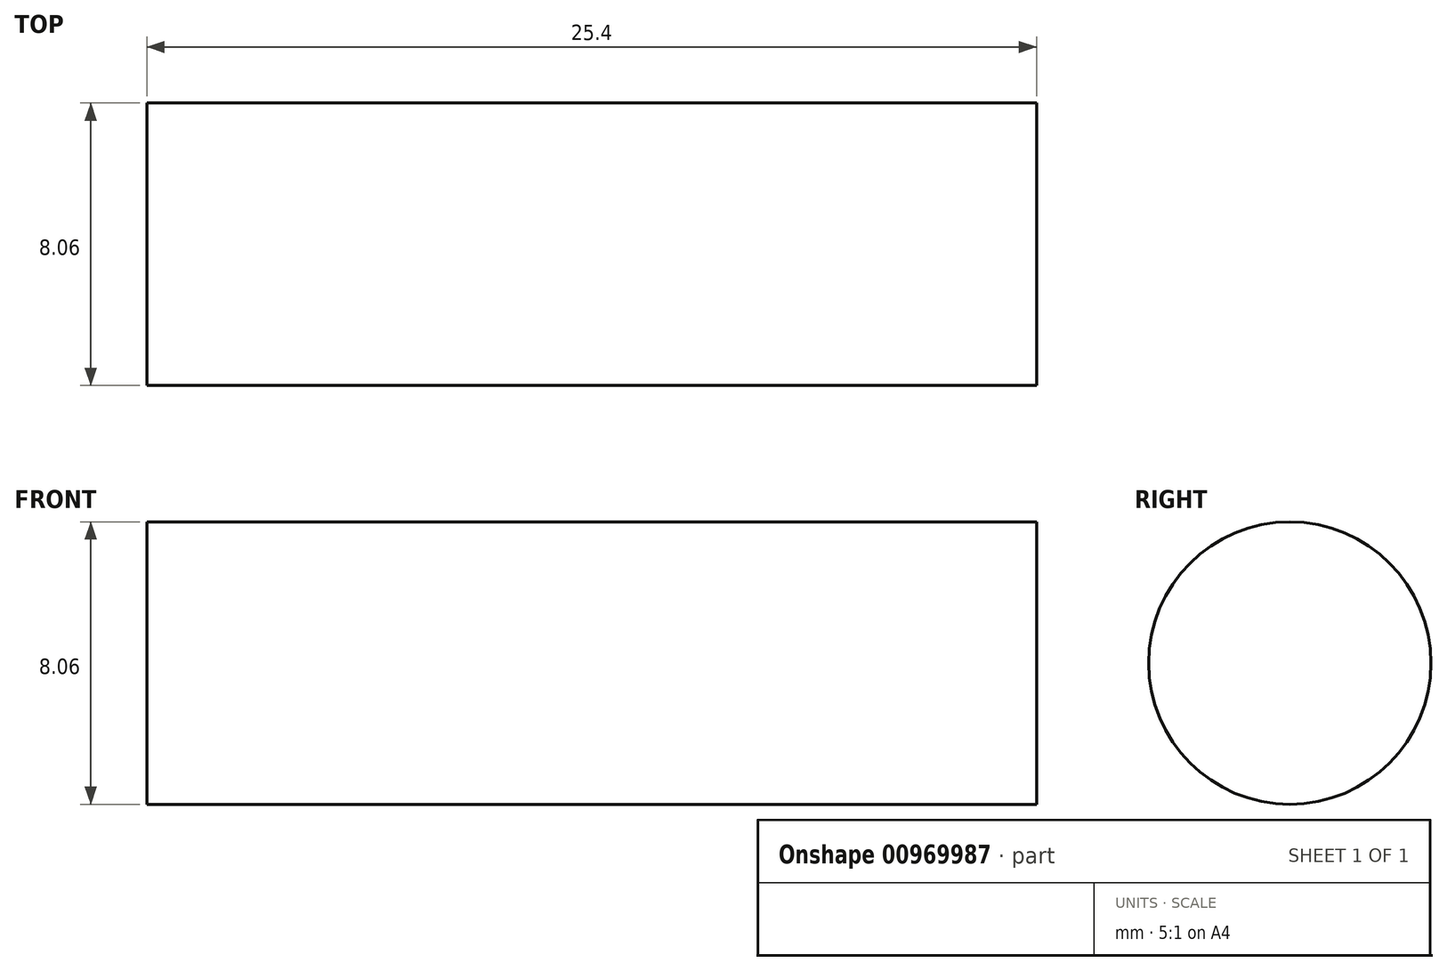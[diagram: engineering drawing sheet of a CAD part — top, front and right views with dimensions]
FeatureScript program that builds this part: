
annotation { "Feature Type Name" : "Feature", "Feature Type Description" : "" }
export const myFeature = defineFeature(function(context is Context, id is Id, definition is map)
    precondition{}
    {
        {
            var Q0;
            Q0=qCreatedBy(makeId("Right.planeOp"),FACE);
            var sketch = newSketch(context, id + "F0", { "sketchPlane" : qUnion([Q0])});
            skCircle(sketch, "E0", {"center": v(0, -49.72) * mm, "radius": 4.03 * mm});
            skSolve(sketch);
        }
        {
            var Q0;
            Q0 = qSketchRegion(id + "F0", true);
            extrude(context, id + "F1", {"entities" : qUnion([Q0]), "depth" : 25.4 * mm, "offsetDistance" : 25.4 * mm});
        }
    });
